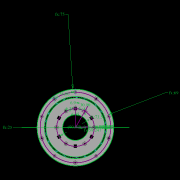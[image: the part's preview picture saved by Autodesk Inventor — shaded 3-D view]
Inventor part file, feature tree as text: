
AUTODESK INVENTOR PART (.ipt)
format: ipt  version: 2022.2 (Build 262287010, 287A)  size: 794,624 bytes
history: native  units: mm
features: extrude x28, other x19, sketch x17, pattern_circular x11, plane x4, fillet x2, move_body x2, revolve x2, draft x2, chamfer x2
ambient origin geometry x8: Origin, YZ Plane, XZ Plane, XY Plane, X Axis, Y Axis, Z Axis, Center Point
bodies: Solid5 (feature_tree)
feature tree (89):
  other  "CrossSection1"
  sketch  "Sketch7"  dims[d167=8.972256mm]
  other  "Roller1"
  other  "Roller2"
  sketch  "Sketch22"  dims[d173=10.814812mm]
  sketch  "Sketch2"  dims[d57=4.025mm d90=61.984365mm]
  sketch  "Sketch23"  dims[d201=75.0mm d232=0.0mm d233=3600.0mm]
  other  "RevRoller1"
  fillet  "Fillet1"  Radius=59.246882mm
  extrude  "Extrusion39"  Depth=61.984365mm
  pattern_circular  "Circular Pattern13"  Count=360  [1 undecoded]
  move_body  "Move Body7"
  revolve  "Revolution13"  [1 undecoded]
  fillet  "Fillet3"  Radius=0.025mm
  pattern_circular  "Circular Pattern14"  Count=24  [1 undecoded]
  move_body  "Move Body6"
  revolve  "Revolution14"  Angle=360.0deg
  other  "OuterRim_Top2"
  other  "OuterRim_Bottom2"
  plane  "Work Plane8"
  sketch  "Sketch49"  dims[d352=0.025mm]
  sketch  "Sketch50"  dims[d354=0.025mm]
  sketch  "Sketch51"  dims[d355=16.1595mm]
  extrude  "Extrusion40"  Depth=0.75mm
  extrude  "Extrusion41"  Depth=0.75mm
  extrude  "Extrusion42"  Depth=0.75mm
  extrude  "Extrusion43"  Depth=0.75mm
  sketch  "Sketch52"  dims[d356=16.159664mm]
  extrude  "Extrusion44"  Depth=0.75mm
  extrude  "Extrusion45"  TaperAngle=90.0deg  [1 undecoded]
  extrude  "Extrusion46"  Depth=0.75mm
  extrude  "Extrusion47"  Depth=0.75mm
  pattern_circular  "Circular Pattern32"  Angle=360.0deg  [1 undecoded]
  pattern_circular  "Circular Pattern33"  Angle=90.0deg  [1 undecoded]
  sketch  "Sketch57"  dims[d358=360.0deg]
  extrude  "Extrusion50"  Depth=0.1mm
  extrude  "Extrusion51"  Depth=0.75mm
  pattern_circular  "Circular Pattern34"  [2 undecoded]
  extrude  "Extrusion52"  Depth=0.75mm
  extrude  "Extrusion53"  Depth=0.75mm
  pattern_circular  "Circular Pattern35"  [2 undecoded]
  plane  "Work Plane7"
  sketch  "Sketch47"  dims[d350=47.575427mm]
  extrude  "Rotor_Ring"  TaperAngle=0.0deg  [1 undecoded]
  draft  "FaceDraft2"
  sketch  "Sketch30"  dims[d343=16.1595mm d344=16.159664mm d345=0.025mm]
  plane  "Work Plane5"
  other  "Rotor Featurs"
  other  "RotorRim_Bottom"
  extrude  "Extrusion24"  TaperAngle=0.0deg  [1 undecoded]
  extrude  "Extrusion25"  Depth=25.0mm
  extrude  "Extrusion26"  Depth=75.0mm
  pattern_circular  "Circular Pattern23"  [2 undecoded]
  sketch  "Sketch41"  dims[d347=0.1mm]
  extrude  "Extrusion27"  Depth=1.5mm
  extrude  "Extrusion28"  Depth=1.5mm
  pattern_circular  "Circular Pattern24"  [2 undecoded]
  extrude  "Extrusion29"  TaperAngle=90.0deg  [1 undecoded]
  extrude  "Extrusion30"  TaperAngle=90.0deg  [1 undecoded]
  extrude  "Extrusion31"  TaperAngle=90.0deg  [1 undecoded]
  pattern_circular  "Circular Pattern25"  [2 undecoded]
  sketch  "Sketch42"  dims[d348=0.1mm]
  extrude  "Extrusion32"  Depth=11.193516mm
  extrude  "Extrusion33"  TaperAngle=0.0deg  [1 undecoded]
  extrude  "Extrusion34"  Depth=0.75mm
  extrude  "Extrusion35"  Depth=2.0mm TaperAngle=0.0deg
  pattern_circular  "Circular Pattern26"  [2 undecoded]
  pattern_circular  "Circular Pattern27"  [2 undecoded]
  chamfer  "Chamfer1"  Distance=8.0mm
  chamfer  "Chamfer2"  Distance=2.5mm Angle=30.0deg
  draft  "FaceDraft4"
  plane  "Work Plane6"
  sketch  "Sketch43"  dims[d349=47.575591mm]
  extrude  "Extrusion37"  Depth=0.75mm
  extrude  "Extrusion38"  Depth=0.75mm TaperAngle=30.0deg
  other  "2D Equation Curve1"
  sketch  "Sketch40"  dims[d346=0.025mm]
  other  "Work Axis6"
  other  "Work Axis7"
  other  "Work Axis8"
  other  "Work Axis9"
  other  "Work Axis10"
  other  "Work Point1"
  other  "Work Point2"
  other  "Work Point3"
  other  "Work Point4"
  other  "Work Point5"
  sketch  "Sketch48"  dims[d351=0.025mm]
  sketch  "Sketch58"  dims[d359=0.5mm d360=240.0mm d361=360.0deg d363=1.308997mm d367=8.1mm d370=0.025mm d371=1.0mm d372=1.308997mm d373=90.0deg d374=0.5mm d375=240.0mm d376=360.0deg d378=90.0deg d379=0.1mm d380=0.025mm d381=0.025mm d382=0.025mm d383=0.025mm d384=11.193516mm d385=0.0mm d386=0.0mm d391=25.0mm d392=75.0mm d393=1.5mm d394=1.5mm d395=1.5mm d396=1.5mm d397=90.0deg d398=90.0deg d399=90.0deg d400=75.0mm d401=11.193516mm d402=0.0mm d486=0.436332mm d487=0.5mm d488=2.0mm d489=0.0mm d490=20.0mm d495=2.5mm d496=8.0mm d506=13.856406mm d507=55.5mm d508=8.0mm d509=0.05mm d510=2.5mm d511=30.0deg d512=12.0mm d513=6.0mm d514=0.2mm d515=30.0deg d516=131.0mm d517=65.5mm d518=0.2mm d519=100.0mm d520=120.0mm d521=2.0mm d522=150.0mm d530=50.0mm d531=5.5mm d532=5.5mm d533=5.5mm d534=85.75mm d535=73.5mm d536=61.25mm d537=24.5mm d538=3.0mm d539=2.4mm d540=0.0mm d541=0.0mm d542=0.0mm d543=5.5mm d544=3.0mm d545=0.0mm d546=90.0mm d547=360.0deg d549=3.0mm d550=3.0mm d551=2.4mm d552=0.0mm d553=5.596758mm d554=0.0mm d555=2.4mm d556=0.0mm d557=5.596758mm d558=0.0mm d559=5.596758mm d560=0.0mm d561=90.0mm d562=360.0deg d564=60.0mm d565=360.0deg d567=5.5mm d568=5.5mm d569=3.0mm d570=0.0mm d571=5.596758mm d572=0.0mm d573=3.0mm d574=0.0mm d575=5.596758mm d576=0.0mm d577=90.0mm d578=360.0deg d580=60.0mm d581=360.0deg d584=20.0mm d585=8.0mm d587=1.75mm d589=3.0mm d592=2.0mm d593=12.0mm d594=12.0mm d600=0.5mm d601=2.0mm d602=45.0deg d603=0.5mm d604=2.0mm d605=45.0deg d606=0.436332mm d607=0.5mm d608=0.0mm d609=20.0mm d611=360.0deg d613=0.0mm d614=0.0mm d617=0.99971mm d618=100.0mm d620=69.0mm d621=5.0mm d622=0.5mm d623=0.5mm d624=5.0mm d625=0.2mm d626=0.0mm d627=20.0mm d629=69.0mm d630=73.5mm d631=20.0mm d633=6.283185mm d635=5.5mm d636=3.0mm d637=7.0mm d638=4.0mm d639=5.596758mm d640=0.0mm d641=3.0mm d642=0.0mm d643=5.596758mm d644=0.0mm d645=4.0mm d646=0.0mm d647=20.0mm d649=6.283185mm d651=3.0mm d652=4.0mm d653=20.0mm d655=6.283185mm d657=7.0mm d658=5.5mm d659=5.596758mm d660=0.0mm d661=2.593516mm d662=0.0mm d663=5.596758mm d664=0.0mm d665=3.193516mm d666=0.0mm d679=50.0mm d680=360.0deg d682=50.0mm d683=360.0deg d694=6.35mm d695=6.35mm d696=6.9mm d697=5.9mm d698=11.194mm d699=0.0mm d700=8.194mm d701=0.0mm d702=60.0mm d703=360.0deg d705=30.0deg d706=4.0mm d707=7.0mm d708=3.193516mm d709=0.0mm d710=11.193516mm d711=0.0mm d712=60.0mm d713=360.0deg d16=0.872665mm d17=0.872665mm d49=0.872665mm d50=0.872665mm d51=0.872665mm d52=0.872665mm d236=0.5mm d237=0.872665mm d238=0.5mm d239=0.872665mm d282=1.0mm d283=1.0mm d284=1.0mm d285=0.15mm d286=0.25mm d287=0.375mm d288=14.3117mm d289=0.75mm d290=20.594885mm d291=0.0625mm d292=0.75mm d293=0.375mm d405=0.5mm d406=0.872665mm d407=0.5mm d408=0.872665mm d413=0.5mm d414=0.872665mm d415=0.5mm d416=0.872665mm d417=0.5mm d418=0.872665mm d419=0.5mm d420=0.872665mm d421=0.872665mm d431=0.5mm d432=0.872665mm d433=0.5mm d434=0.872665mm d471=0.5mm d472=0.872665mm d473=0.5mm d474=0.872665mm d497=0.5mm d498=0.872665mm d499=0.5mm d500=0.872665mm d590=0.5mm d591=0.872665mm]
note: 26 required parameter values undecoded (feature->parameter linkage not recoverable at this tier; creation-order binding heuristic only, values carry confidence <= 0.55)